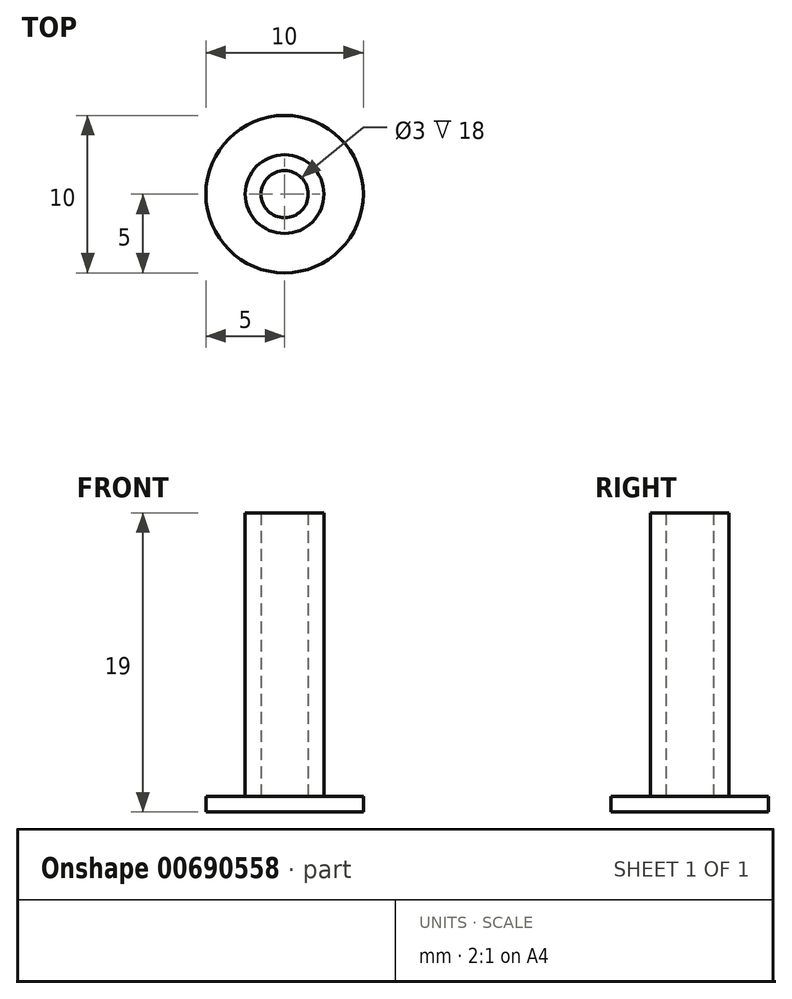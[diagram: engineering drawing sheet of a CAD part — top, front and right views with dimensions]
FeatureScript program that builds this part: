
annotation { "Feature Type Name" : "Feature", "Feature Type Description" : "" }
export const myFeature = defineFeature(function(context is Context, id is Id, definition is map)
    precondition{}
    {
        {
            var Q0;
            Q0=qCreatedBy(makeId("Top.planeOp"),FACE);
            var sketch = newSketch(context, id + "F0", { "sketchPlane" : qUnion([Q0])});
            skCircle(sketch, "E0", {"center": v(0, 0) * mm, "radius": 2.5 * mm});
            skCircle(sketch, "E1", {"center": v(0, 0) * mm, "radius": 1.5 * mm});
            skSolve(sketch);
        }
        {
            var Q0;
            Q0=makeQuery(id+"F0.imprint","IMPRINT",FACE,{"disambiguationData":[TD([[makeQuery(id+"F0.imprint","IMPRINT",EDGE,{"derivedFrom":sQuery(id+"F0.wireOp",EDGE,"E0")}),1.0]])]});
            extrude(context, id + "F1", {"entities" : qUnion([Q0]), "depth" : 18 * mm, "offsetDistance" : 25 * mm});
        }
        {
            var Q0;
            Q0=qCreatedBy(makeId("Top.planeOp"),FACE);
            var sketch = newSketch(context, id + "F2", { "sketchPlane" : qUnion([Q0])});
            skCircle(sketch, "E2", {"center": v(0, 0) * mm, "radius": 5 * mm});
            skSolve(sketch);
        }
        {
            var Q0;
            Q0=makeQuery(id+"F2.imprint","IMPRINT",FACE,{"disambiguationData":[TD([[makeQuery(id+"F2.imprint","IMPRINT",EDGE,{"derivedFrom":sQuery(id+"F2.wireOp",EDGE,"E2")}),1.0]])]});
            extrude(context, id + "F3", {"entities" : qUnion([Q0]), "operationType" : NewBodyOperationType.ADD, "oppositeDirection" : true, "depth" : 1 * mm, "offsetDistance" : 25 * mm});
        }
    });
